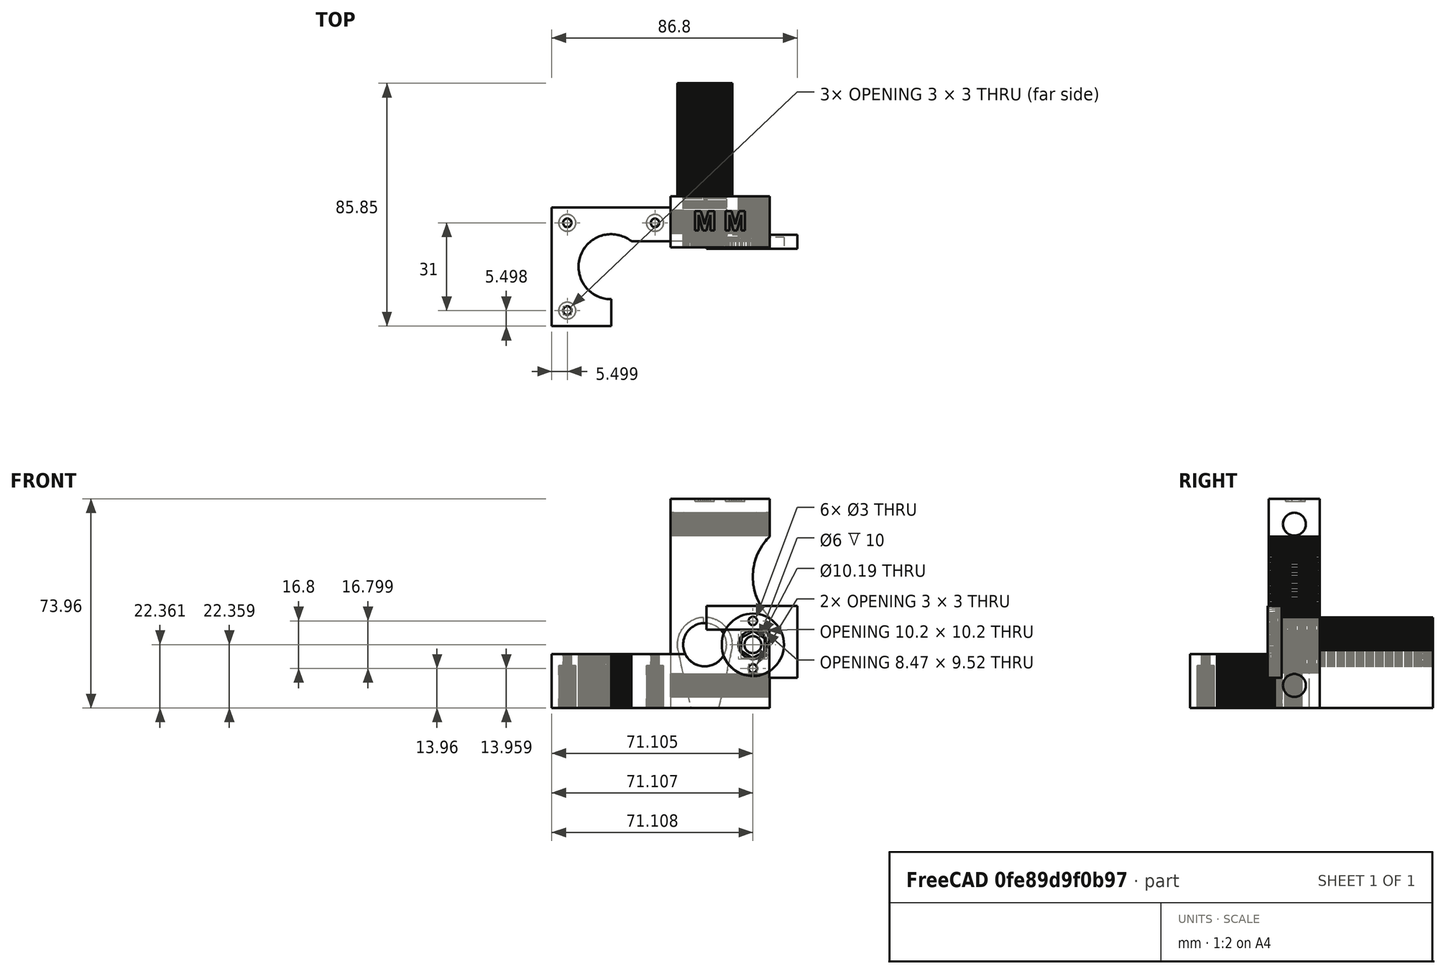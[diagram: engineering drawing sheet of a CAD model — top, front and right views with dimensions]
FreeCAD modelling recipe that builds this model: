
FCSTD DOCUMENT  (FreeCAD 0.16R6045 (Git))
Label: Adaptador-HusilloVarilla
License: All rights reserved
LicenseURL: http://en.wikipedia.org/wiki/All_rights_reserved
objects: Sketcher::SketchObject×5, PartDesign::Pad×2, Part::Feature×1, Part::Extrusion×1, PartDesign::Pocket×1
note: 13 computed .brp shape members not serialized (recipe doc carries the construction recipe); baked Part::Feature solids carry a one-line shape summary decoded from their .brp

FEATURE [Part::Feature] Solid
  shape: bbox 77 x 85.85 x 73.96 mm, 8522 faces (baked)
FEATURE [Sketcher::SketchObject] Sketch
  ExternalGeometry = -> [Solid]
  Placement = pos=(0,-4608.23,0) rot=(1,0,0;1.5708rad)
  Support = -> Solid [Face521]
  sketch-geometry (5):
    g0: Circle [constr] CenterX=5799.88 CenterY=230.838 CenterZ=0 NormalX=0 NormalY=0 NormalZ=1 Radius=11.1007
    g1: Circle CenterX=5799.88 CenterY=230.841 CenterZ=0 NormalX=0 NormalY=0 NormalZ=1 Radius=5.09695
    g2: Circle CenterX=5799.88 CenterY=230.838 CenterZ=0 NormalX=0 NormalY=0 NormalZ=1 Radius=11
    g3: Circle CenterX=5799.88 CenterY=222.44 CenterZ=0 NormalX=0 NormalY=0 NormalZ=1 Radius=1.50087
    g4: Circle CenterX=5799.88 CenterY=239.238 CenterZ=0 NormalX=0 NormalY=0 NormalZ=1 Radius=1.5006
  constraints (14):
    c: PointOnObject(g-6,g0)
    c: PointOnObject(g-7,g0)
    c: PointOnObject(g-5,g0)
    c: PointOnObject(g-9,g1)
    c: PointOnObject(g-8,g1)
    c: PointOnObject(g-10,g1)
    c: Coincident(g2,g0)
    c: Radius(g2) = 11
    c: PointOnObject(g-12,g3)
    c: PointOnObject(g-11,g3)
    c: PointOnObject(g-13,g3)
    c: PointOnObject(g-16,g4)
    c: PointOnObject(g-15,g4)
    c: PointOnObject(g-14,g4)
FEATURE [Part::Extrusion] Extrude
  Base = -> Sketch
  Dir = (0,-4,0)
  Solid = true
FEATURE [Sketcher::SketchObject] Sketch001
  ExternalGeometry = -> [Extrude]
  Placement = pos=(0,-4612.23,0) rot=(1,0,0;1.5708rad)
  Support = -> Extrude [Face6]
  sketch-geometry (8):
    g0: Circle CenterX=5799.88 CenterY=230.841 CenterZ=0 NormalX=0 NormalY=0 NormalZ=1 Radius=5.09695
    g1: LineSegment StartX=5804.11 StartY=233.02 StartZ=0 EndX=5800.11 EndY=235.598 EndZ=0
    g2: LineSegment StartX=5800.11 StartY=235.598 StartZ=0 EndX=5795.87 EndY=233.419 EndZ=0
    g3: LineSegment StartX=5795.87 StartY=233.419 StartZ=0 EndX=5795.64 EndY=228.661 EndZ=0
    g4: LineSegment StartX=5795.64 StartY=228.661 StartZ=0 EndX=5799.64 EndY=226.083 EndZ=0
    g5: LineSegment StartX=5799.64 StartY=226.083 StartZ=0 EndX=5803.88 EndY=228.263 EndZ=0
    g6: LineSegment StartX=5803.88 StartY=228.263 StartZ=0 EndX=5804.11 EndY=233.02 EndZ=0
    g7: Circle [constr] CenterX=5799.88 CenterY=230.841 CenterZ=0 NormalX=0 NormalY=0 NormalZ=1 Radius=4.76314
  constraints (18):
    c: Coincident(g0,g-5)
    c: Coincident(g1,g2)
    c: Coincident(g2,g3)
    c: Coincident(g3,g4)
    c: Coincident(g4,g5)
    c: Coincident(g5,g6)
    c: Coincident(g6,g1)
    c: Equal(g1, g2-g6) x5
    c: PointOnObject(g1,g7)
    c: PointOnObject(g2,g7)
    c: PointOnObject(g3,g7)
    c: PointOnObject(g4,g7)
    c: PointOnObject(g5,g7)
    c: PointOnObject(g6,g7)
    c: Coincident(g4,g0)
    c: Coincident(g0,g7)
    c: Distance(g5,g3) = 8.25
    c: Equal(g0,g-5)
FEATURE [PartDesign::Pad] Pad
  Length = 4
  Length2 = 100
  Reversed = true
  Sketch = -> Sketch001
  Type = 0
FEATURE [Sketcher::SketchObject] Sketch002
  ExternalGeometry = -> [Pad]
  Placement = pos=(0,-4608.23,0) rot=(0,0.707107,0.707107;3.14159rad)
  Support = -> Pad [Face5]
  sketch-geometry (2):
    g0: Circle CenterX=-5799.88 CenterY=230.841 CenterZ=0 NormalX=0 NormalY=0 NormalZ=1 Radius=3
    g1: Circle CenterX=-5799.88 CenterY=230.841 CenterZ=0 NormalX=0 NormalY=0 NormalZ=1 Radius=4.84435
  constraints (3):
    c: Coincident(g0,g-3)
    c: Coincident(g1,g0)
    c: Radius(g0) = 3
FEATURE [PartDesign::Pad] Pad001
  Length = 10
  Length2 = 100
  Sketch = -> Sketch002
  Type = 0
FEATURE [Sketcher::SketchObject] Sketch003
  ExternalGeometry = -> [Pad001]
  Placement = pos=(0,-4612.23,0) rot=(1,0,0;1.5708rad)
  Support = -> Pad001 [Face3]
  sketch-geometry (9):
    g0: LineSegment [constr] StartX=5799.88 StartY=239.238 StartZ=0 EndX=5799.88 EndY=222.44 EndZ=0
    g1: LineSegment StartX=5805.72 StartY=244.53 StartZ=0 EndX=5815.57 EndY=244.53 EndZ=0
    g2: LineSegment StartX=5815.57 StartY=244.53 StartZ=0 EndX=5815.57 EndY=219.137 EndZ=0
    g3: LineSegment StartX=5815.57 StartY=219.137 StartZ=0 EndX=5805.72 EndY=219.137 EndZ=0
    g4: LineSegment StartX=5805.72 StartY=219.137 StartZ=0 EndX=5805.72 EndY=236.17 EndZ=0
    g5: LineSegment [constr] StartX=5804.72 StartY=240.715 StartZ=0 EndX=5804.72 EndY=220.961 EndZ=0
    g6: LineSegment StartX=5805.72 StartY=244.53 StartZ=0 EndX=5783.41 EndY=244.53 EndZ=0
    g7: LineSegment StartX=5783.41 StartY=244.53 StartZ=0 EndX=5783.41 EndY=236.17 EndZ=0
    g8: LineSegment StartX=5783.41 StartY=236.17 StartZ=0 EndX=5805.72 EndY=236.17 EndZ=0
  constraints (21):
    c: Coincident(g0,g-5)
    c: Coincident(g0,g-6)
    c: Coincident(g1,g2)
    c: Coincident(g2,g3)
    c: Coincident(g3,g4)
    c: Horizontal(g1)
    c: Horizontal(g3)
    c: Vertical(g2)
    c: Vertical(g4)
    c: PointOnObject(g5,g-7)
    c: PointOnObject(g5,g-7)
    c: Vertical(g5)
    c: Tangent(g-3,g5)
    c: Distance(g5,g4) = 1
    c: Coincident(g1,g6)
    c: Horizontal(g6)
    c: Coincident(g6,g7)
    c: Vertical(g7)
    c: Coincident(g7,g8)
    c: Horizontal(g8)
    c: Coincident(g4,g8)
FEATURE [PartDesign::Pocket] Pocket
  Length = 5
  Sketch = -> Sketch003
  Type = 0
FEATURE [Sketcher::SketchObject] Sketch004
  ExternalGeometry = -> [Pocket]
  Placement = pos=(0,-4608.23,0) rot=(0,0.707107,0.707107;3.14159rad)
  Support = -> Pocket [Face2]
  sketch-geometry (4):
    g0: LineSegment StartX=-5809.46 StartY=248.646 StartZ=0 EndX=-5785.33 EndY=248.646 EndZ=0
    g1: LineSegment StartX=-5785.33 StartY=248.646 StartZ=0 EndX=-5785.33 EndY=235.938 EndZ=0
    g2: LineSegment StartX=-5785.33 StartY=235.938 StartZ=0 EndX=-5809.46 EndY=235.938 EndZ=0
    g3: LineSegment StartX=-5809.46 StartY=235.938 StartZ=0 EndX=-5809.46 EndY=248.646 EndZ=0
  constraints (9):
    c: Coincident(g0,g1)
    c: Coincident(g1,g2)
    c: Coincident(g2,g3)
    c: Coincident(g3,g0)
    c: Horizontal(g0)
    c: Horizontal(g2)
    c: Vertical(g1)
    c: Vertical(g3)
    c: Tangent(g-3,g2)
